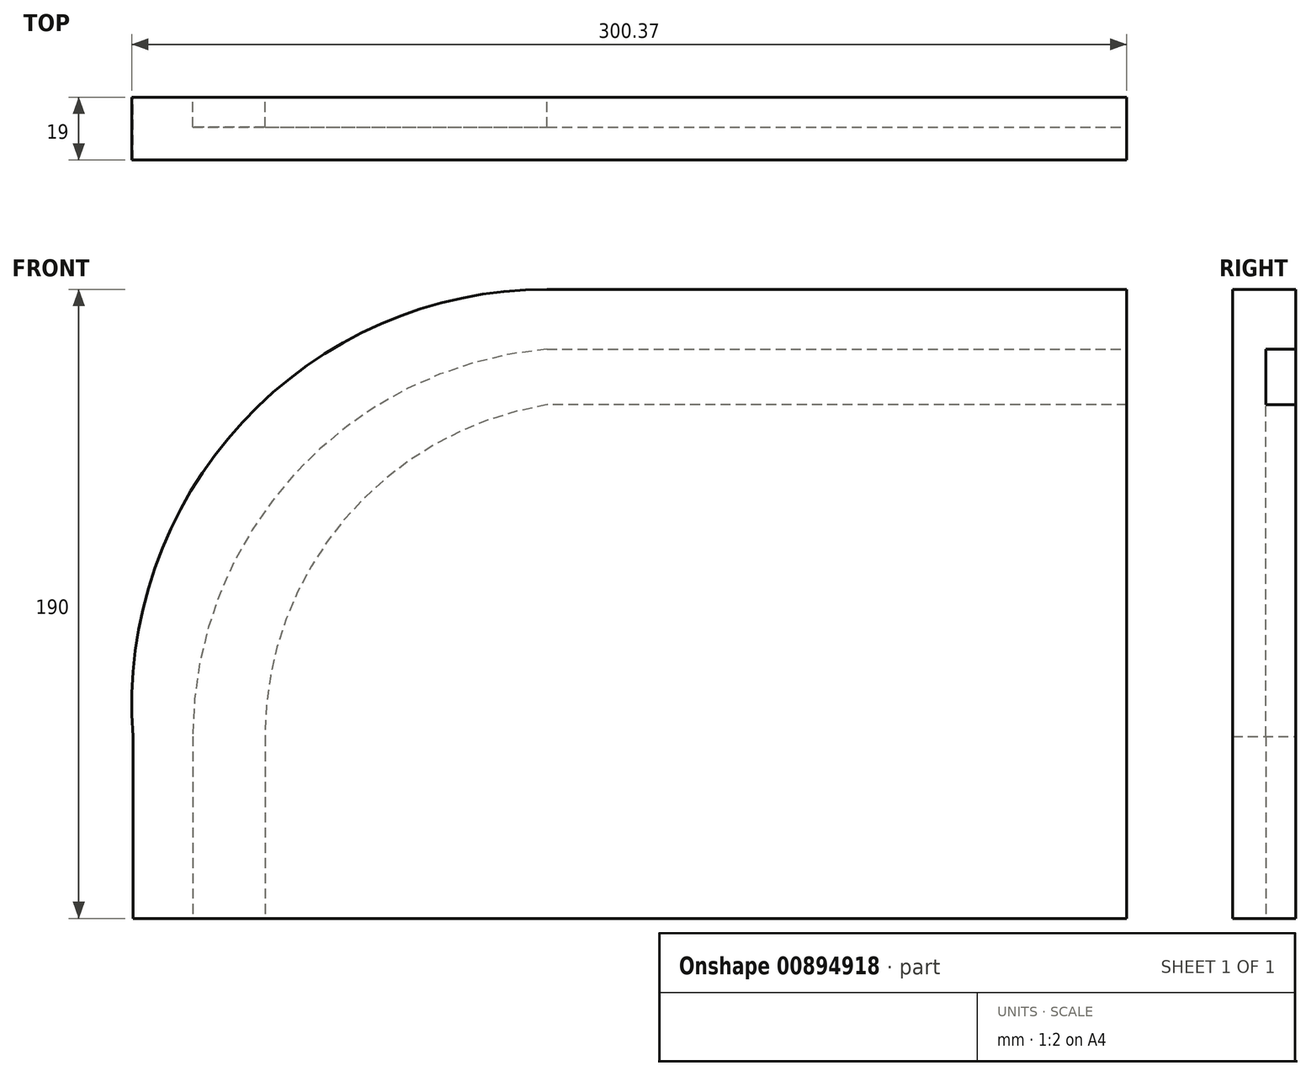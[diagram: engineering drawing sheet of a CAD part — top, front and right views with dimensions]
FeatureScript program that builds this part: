
annotation { "Feature Type Name" : "Feature", "Feature Type Description" : "" }
export const myFeature = defineFeature(function(context is Context, id is Id, definition is map)
    precondition{}
    {
        {
            var Q0;
            Q0=qCreatedBy(makeId("Front.planeOp"),FACE);
            var sketch = newSketch(context, id + "F0", { "sketchPlane" : qUnion([Q0])});
            skLineSegment(sketch, "E0", {"start": v(300, -155.09) * mm, "end": v(0, -155.09) * mm});
            skLineSegment(sketch, "E1", {"start": v(0, -155.09) * mm, "end": v(0, -100.09) * mm});
            skLineSegment(sketch, "E2", {"start": v(300, -155.09) * mm, "end": v(300, 34.91) * mm});
            skLineSegment(sketch, "E3", {"start": v(300, 34.91) * mm, "end": v(125, 34.91) * mm});
            skArc(sketch, "E4", {"start": v(125, 34.91) * mm, "mid": v(33, -5.28) * mm, "end": v(0, -100.09) * mm});
            skSolve(sketch);
        }
        {
            var Q0;
            Q0=makeQuery(id+"F0.imprint","IMPRINT",FACE,{"disambiguationData":[TD([[makeQuery(id+"F0.imprint","IMPRINT",EDGE,{"derivedFrom":sQuery(id+"F0.wireOp",EDGE,"E0")}),-1.0]])]});
            extrude(context, id + "F1", {"entities" : qUnion([Q0]), "depth" : 19 * mm, "offsetDistance" : 25.4 * mm});
        }
        {
            var Q0;
            Q0=makeQuery(id+"F1.opExtrude","CAP_FACE",FACE,{"disambiguationData":[OSD([sQuery(id+"F0.wireOp",EDGE,"E0"),sQuery(id+"F0.wireOp",EDGE,"E1"),sQuery(id+"F0.wireOp",EDGE,"E2"),sQuery(id+"F0.wireOp",EDGE,"E3"),sQuery(id+"F0.wireOp",EDGE,"E4")])],"isStart":true});
            var sketch = newSketch(context, id + "F2", { "sketchPlane" : qUnion([Q0])});
            skPoint(sketch, "E5", {"position": v(-300, 0) * mm});
            skPoint(sketch, "E6", {"position": v(-300, 16.87) * mm});
            skPoint(sketch, "E7", {"position": v(-18.05, -155.09) * mm});
            skPoint(sketch, "E8", {"position": v(-39.83, -155.09) * mm});
            skPoint(sketch, "E9", {"position": v(-18.05, -100.09) * mm});
            skPoint(sketch, "E10", {"position": v(-39.83, -100.09) * mm});
            skPoint(sketch, "E11", {"position": v(-125, 16.87) * mm});
            skPoint(sketch, "E12", {"position": v(-125, 0) * mm});
            skLineSegment(sketch, "E13", {"start": v(-300, 0) * mm, "end": v(-125, 0) * mm});
            skLineSegment(sketch, "E14", {"start": v(-125, 16.87) * mm, "end": v(-300, 16.87) * mm});
            skLineSegment(sketch, "E15", {"start": v(-39.83, -100.09) * mm, "end": v(-39.83, -155.09) * mm});
            skLineSegment(sketch, "E16", {"start": v(-18.05, -100.09) * mm, "end": v(-18.05, -155.09) * mm});
            skArc(sketch, "E17", {"start": v(-18.05, -100.09) * mm, "mid": v(-48.82, -20.85) * mm, "end": v(-125, 16.87) * mm});
            skArc(sketch, "E18", {"start": v(-39.83, -100.09) * mm, "mid": v(-64, -34.38) * mm, "end": v(-125, 0) * mm});
            skSolve(sketch);
        }
        {
            var Q0;
            {var subQ1=sQuery(id+"F2.wireOp",EDGE,"E13");Q0=makeQuery(id+"F2.imprint","IMPRINT",FACE,{"disambiguationData":[TD([[makeQuery(id+"F2.imprint","IMPRINT",EDGE,{"derivedFrom":subQ1}),1.0]])]});}
            extrude(context, id + "F3", {"entities" : qUnion([Q0]), "operationType" : NewBodyOperationType.REMOVE, "oppositeDirection" : true, "depth" : 9 * mm, "offsetDistance" : 25.4 * mm});
        }
    });
